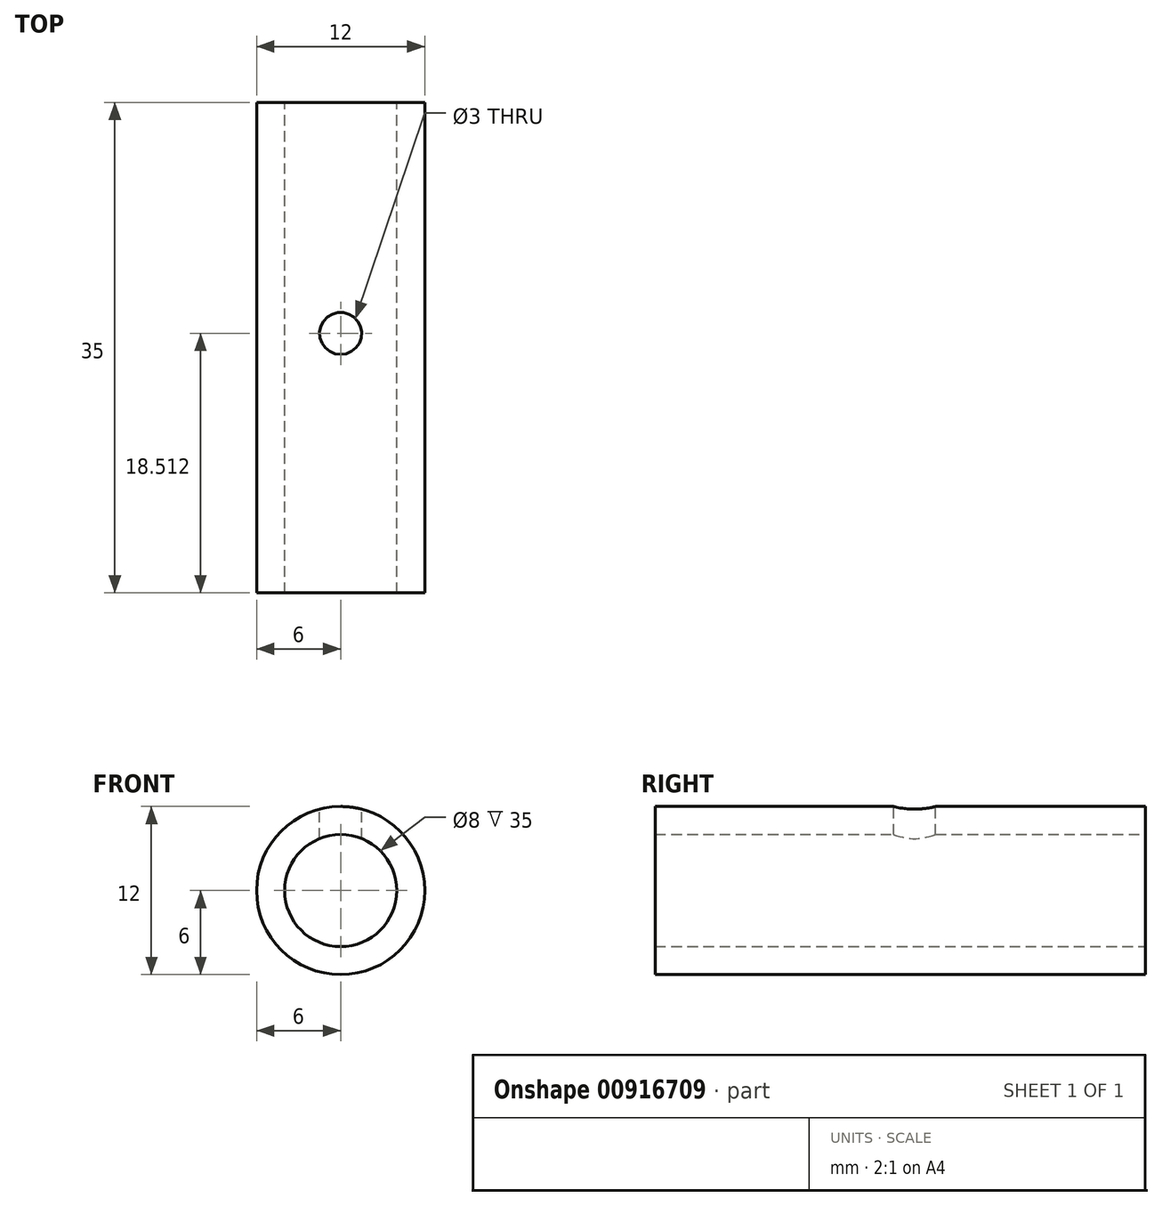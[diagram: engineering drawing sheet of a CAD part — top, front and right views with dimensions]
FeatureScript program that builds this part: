
annotation { "Feature Type Name" : "Feature", "Feature Type Description" : "" }
export const myFeature = defineFeature(function(context is Context, id is Id, definition is map)
    precondition{}
    {
        {
            var Q0;
            Q0=qCreatedBy(makeId("Front.planeOp"),FACE);
            var sketch = newSketch(context, id + "F0", { "sketchPlane" : qUnion([Q0])});
            skCircle(sketch, "E0", {"center": v(0, 0) * mm, "radius": 4 * mm});
            skCircle(sketch, "E1", {"center": v(0, 0) * mm, "radius": 6 * mm});
            skSolve(sketch);
        }
        {
            var Q0;
            Q0=qCreatedBy(makeId("Top.planeOp"),FACE);
            var sketch = newSketch(context, id + "F1", { "sketchPlane" : qUnion([Q0])});
            skLineSegment(sketch, "E2", {"start": v(0, 0) * mm, "end": v(0, 35) * mm});
            skSolve(sketch);
        }
        {
            var Q0;
            Q0=makeQuery(id+"F0.imprint","IMPRINT",FACE,{"disambiguationData":[TD([[makeQuery(id+"F0.imprint","IMPRINT",EDGE,{"derivedFrom":sQuery(id+"F0.wireOp",EDGE,"E0")}),-1.0]])]});
            var Q1;
            Q1=sQuery(id+"F1.wireOp",EDGE,"E2");
            sweep(context, id + "F2", {"profiles" : qUnion([Q0]), "path" : qUnion([Q1])});
        }
        {
            var Q0;
            Q0=qCreatedBy(makeId("Top.planeOp"),FACE);
            var sketch = newSketch(context, id + "F3", { "sketchPlane" : qUnion([Q0])});
            skCircle(sketch, "E3", {"center": v(0, 18.51) * mm, "radius": 1.5 * mm});
            skSolve(sketch);
        }
        {
            var Q0;
            Q0=qCreatedBy(makeId("Front.planeOp"),FACE);
            var sketch = newSketch(context, id + "F4", { "sketchPlane" : qUnion([Q0])});
            skLineSegment(sketch, "E4", {"start": v(-2.4, 0) * mm, "end": v(-2.4, 15) * mm});
            skSolve(sketch);
        }
        {
            var Q0;
            Q0 = qSketchRegion(id + "F3", true);
            var Q1;
            Q1 = qConstructionFilter(qBodyType(qCreatedBy(id + "F4" ,EDGE), BodyType.WIRE), ConstructionObject.NO);
            sweep(context, id + "F5", {"operationType" : NewBodyOperationType.REMOVE, "profiles" : qUnion([Q0]), "path" : qUnion([Q1])});
        }
    });
